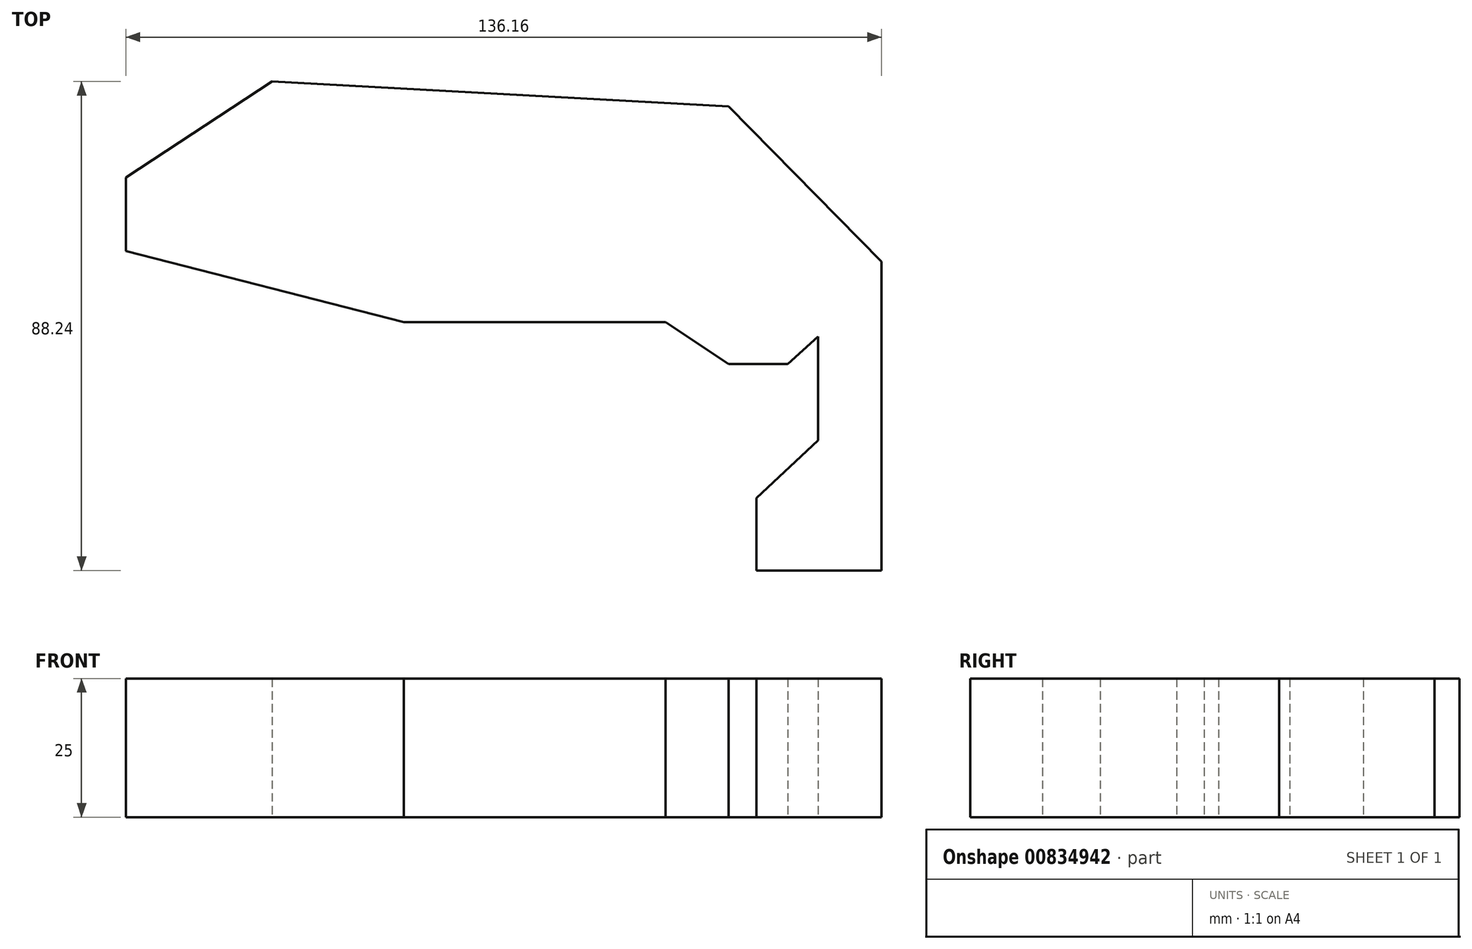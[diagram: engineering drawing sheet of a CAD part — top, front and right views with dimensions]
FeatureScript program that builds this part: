
annotation { "Feature Type Name" : "Feature", "Feature Type Description" : "" }
export const myFeature = defineFeature(function(context is Context, id is Id, definition is map)
    precondition{}
    {
        {
            var Q0;
            Q0=qCreatedBy(makeId("Top.planeOp"),FACE);
            var sketch = newSketch(context, id + "F0", { "sketchPlane" : qUnion([Q0])});
            skLineSegment(sketch, "E0", {"start": v(-61.32, 2.5) * mm, "end": v(-34.99, 19.8) * mm});
            skLineSegment(sketch, "E1", {"start": v(-61.32, 2.5) * mm, "end": v(-61.32, -10.8) * mm});
            skLineSegment(sketch, "E2", {"start": v(-61.32, -10.8) * mm, "end": v(-11.27, -23.6) * mm});
            skLineSegment(sketch, "E3", {"start": v(-11.27, -23.6) * mm, "end": v(35.94, -23.6) * mm});
            skLineSegment(sketch, "E4", {"start": v(35.94, -23.6) * mm, "end": v(47.32, -31.2) * mm});
            skLineSegment(sketch, "E5", {"start": v(47.32, -31.2) * mm, "end": v(58, -31.2) * mm});
            skLineSegment(sketch, "E6", {"start": v(58, -31.2) * mm, "end": v(63.45, -26.21) * mm});
            skLineSegment(sketch, "E7", {"start": v(63.45, -26.21) * mm, "end": v(63.45, -44.95) * mm});
            skLineSegment(sketch, "E8", {"start": v(63.45, -44.95) * mm, "end": v(52.3, -55.39) * mm});
            skLineSegment(sketch, "E9", {"start": v(52.3, -55.39) * mm, "end": v(52.3, -68.43) * mm});
            skLineSegment(sketch, "E10", {"start": v(52.3, -68.43) * mm, "end": v(74.84, -68.43) * mm});
            skLineSegment(sketch, "E11", {"start": v(74.84, -68.43) * mm, "end": v(74.84, -12.7) * mm});
            skLineSegment(sketch, "E12", {"start": v(74.84, -12.7) * mm, "end": v(47.32, 15.3) * mm});
            skLineSegment(sketch, "E13", {"start": v(47.32, 15.3) * mm, "end": v(-34.99, 19.8) * mm});
            skSolve(sketch);
        }
        {
            var Q0;
            Q0=makeQuery(id+"F0.imprint","IMPRINT",FACE,{"disambiguationData":[TD([[makeQuery(id+"F0.imprint","IMPRINT",EDGE,{"derivedFrom":sQuery(id+"F0.wireOp",EDGE,"E0")}),-1.0]])]});
            extrude(context, id + "F1", {"entities" : qUnion([Q0]), "depth" : 25 * mm, "offsetDistance" : 25 * mm});
        }
    });
